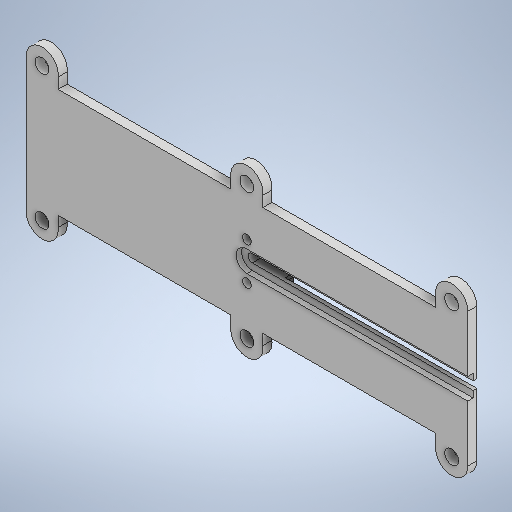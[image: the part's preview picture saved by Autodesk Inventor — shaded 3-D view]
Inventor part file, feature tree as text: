
AUTODESK INVENTOR PART (.ipt)
format: ipt  version: 2025.1 (Build 291241000, 241)  size: 339,456 bytes
history: native  units: mm
features: extrude x4, sketch x4
ambient origin geometry x8: Origin, YZ Plane, XZ Plane, XY Plane, X Axis, Y Axis, Z Axis, Center Point
bodies: Solid1 (feature_tree)
feature tree (8):
  extrude  "Extrusion1"  Depth=15.5mm
  extrude  "Extrusion2"  Depth=2.48mm
  extrude  "Extrusion3"  Depth=10.5mm
  extrude  "Extrusion4"  Depth=20.0mm
  sketch  "Sketch1"  dims[d0=2.48mm d1=15.5mm]
  sketch  "Sketch2"  dims[d2=15.5mm d3=2.48mm]
  sketch  "Sketch3"  dims[d4=10.5mm d5=10.5mm]
  sketch  "Sketch4"  dims[d6=20.0mm d7=20.0mm d8=2.65mm d9=7.25mm d10=2.8mm d11=0.0mm d12=2.5mm d13=33.2mm d14=25.0mm d15=4.9mm d16=4.2mm d17=7.3mm d18=2.75mm d19=0.0mm d20=3.25mm d21=1.65mm d22=0.0mm d25=134.5mm d26=11.75mm d27=14.25mm d28=5.1mm d29=6.6mm d30=8.8mm d31=1.5mm d32=5.1mm d34=8.8mm d35=1.5mm d36=2.3mm d37=0.0mm d38=4.9mm d39=4.2mm]
